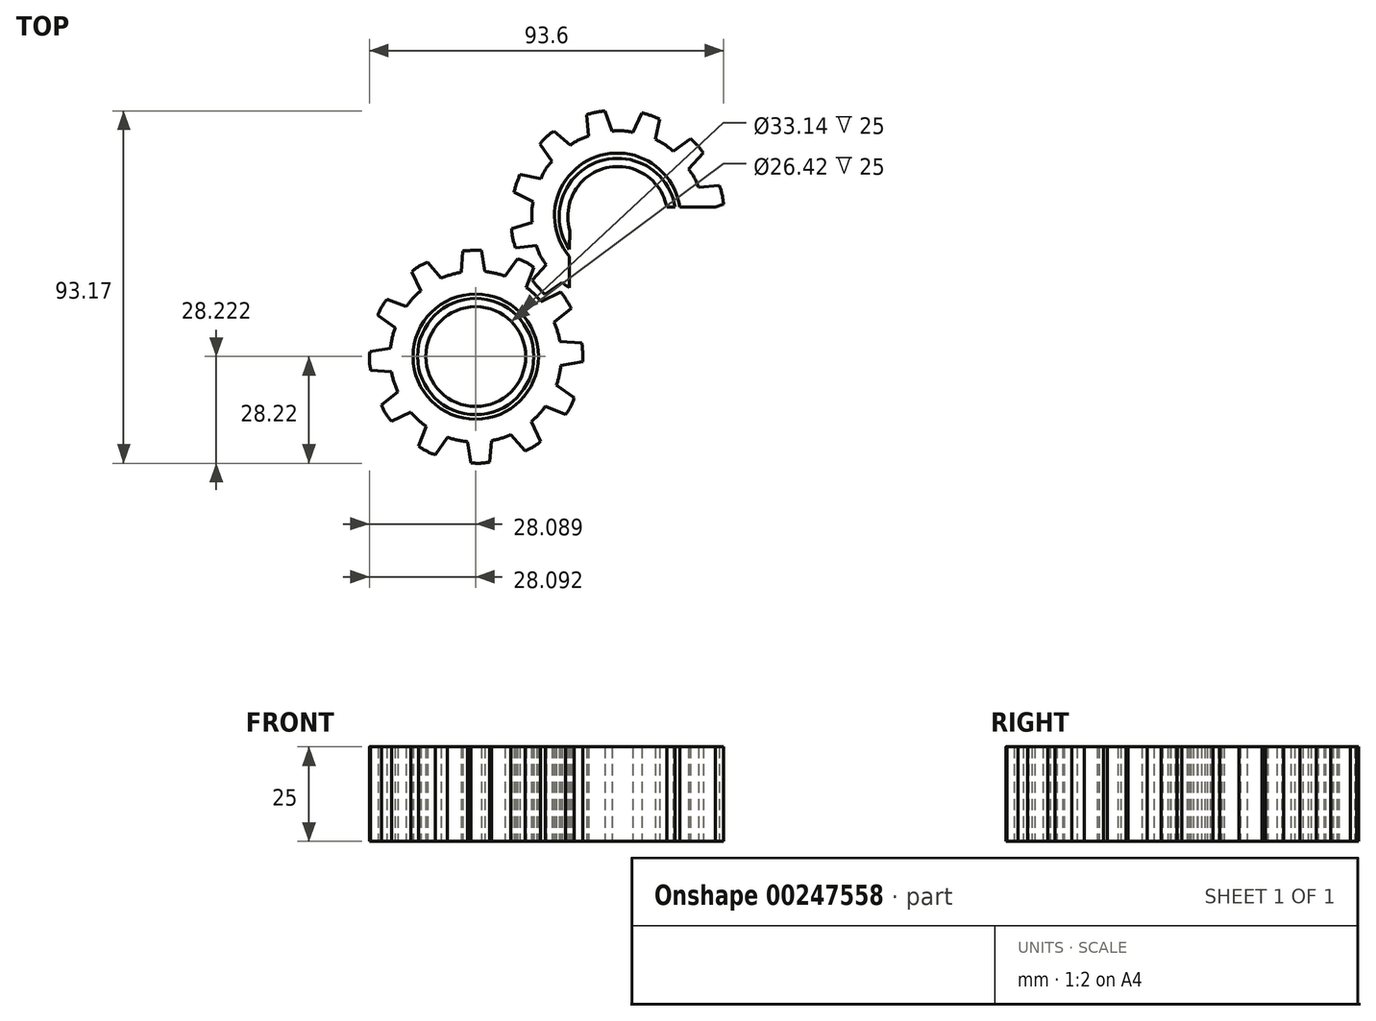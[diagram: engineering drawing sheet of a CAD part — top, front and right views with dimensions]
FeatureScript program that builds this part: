
annotation { "Feature Type Name" : "Feature", "Feature Type Description" : "" }
export const myFeature = defineFeature(function(context is Context, id is Id, definition is map)
    precondition{}
    {
        {
            var Q0;
            Q0=qCreatedBy(makeId("Top.planeOp"),FACE);
            var sketch = newSketch(context, id + "F0", { "sketchPlane" : qUnion([Q0])});
            skPoint(sketch, "E0", {"position": v(-30.45, 10.62) * mm});
            skPoint(sketch, "E1", {"position": v(-30.54, 5.58) * mm});
            skPoint(sketch, "E2", {"position": v(-30.54, 3.71) * mm});
            skPoint(sketch, "E3", {"position": v(-30.54, -4.5) * mm});
            skPoint(sketch, "E4", {"position": v(-4.8, 16.75) * mm});
            skPoint(sketch, "E5", {"position": v(-2.6, 16.75) * mm});
            skPoint(sketch, "E6", {"position": v(-1.42, 16.75) * mm});
            skPoint(sketch, "E7", {"position": v(8.01, 16.75) * mm});
            skPoint(sketch, "E8", {"position": v(10.19, 17.58) * mm});
            skPoint(sketch, "E9", {"position": v(9.1, 22.45) * mm});
            skPoint(sketch, "E10", {"position": v(3.62, 21.97) * mm});
            skPoint(sketch, "E11", {"position": v(0.93, 26.8) * mm});
            skPoint(sketch, "E12", {"position": v(4.81, 31.12) * mm});
            skPoint(sketch, "E13", {"position": v(1.46, 34.84) * mm});
            skPoint(sketch, "E14", {"position": v(-3.18, 31.55) * mm});
            skPoint(sketch, "E15", {"position": v(-7.79, 34.66) * mm});
            skPoint(sketch, "E16", {"position": v(-6.65, 40.1) * mm});
            skPoint(sketch, "E17", {"position": v(-11.41, 41.7) * mm});
            skPoint(sketch, "E18", {"position": v(-13.75, 36.5) * mm});
            skPoint(sketch, "E19", {"position": v(-19.29, 36.84) * mm});
            skPoint(sketch, "E20", {"position": v(-21.12, 42.19) * mm});
            skPoint(sketch, "E21", {"position": v(-26.03, 41.2) * mm});
            skPoint(sketch, "E22", {"position": v(-25.51, 35.54) * mm});
            skPoint(sketch, "E23", {"position": v(-30.37, 33.11) * mm});
            skPoint(sketch, "E24", {"position": v(-34.69, 36.84) * mm});
            skPoint(sketch, "E25", {"position": v(-38.36, 33.48) * mm});
            skPoint(sketch, "E26", {"position": v(-35.15, 28.85) * mm});
            skPoint(sketch, "E27", {"position": v(-38.07, 24.3) * mm});
            skPoint(sketch, "E28", {"position": v(-43.6, 25.41) * mm});
            skPoint(sketch, "E29", {"position": v(-45.2, 20.68) * mm});
            skPoint(sketch, "E30", {"position": v(-40.11, 18.23) * mm});
            skPoint(sketch, "E31", {"position": v(-40.4, 12.78) * mm});
            skPoint(sketch, "E32", {"position": v(-45.77, 11.02) * mm});
            skPoint(sketch, "E33", {"position": v(-44.74, 6.06) * mm});
            skPoint(sketch, "E34", {"position": v(-39.26, 6.63) * mm});
            skPoint(sketch, "E35", {"position": v(-36.68, 1.59) * mm});
            skPoint(sketch, "E36", {"position": v(-40.4, -2.55) * mm});
            skPoint(sketch, "E37", {"position": v(-37.07, -6.32) * mm});
            skPoint(sketch, "E38", {"position": v(-32.47, -3.12) * mm});
            skLineSegment(sketch, "E39", {"start": v(-30.45, 10.62) * mm, "end": v(-30.54, 5.58) * mm});
            skLineSegment(sketch, "E40", {"start": v(-30.54, 3.71) * mm, "end": v(-30.54, -4.5) * mm});
            skLineSegment(sketch, "E41", {"start": v(-4.8, 16.75) * mm, "end": v(-2.6, 16.75) * mm});
            skLineSegment(sketch, "E42", {"start": v(-1.42, 16.75) * mm, "end": v(8.01, 16.75) * mm});
            skLineSegment(sketch, "E43", {"start": v(8.01, 16.75) * mm, "end": v(10.19, 17.58) * mm});
            skLineSegment(sketch, "E44", {"start": v(3.62, 21.97) * mm, "end": v(9.1, 22.45) * mm});
            skLineSegment(sketch, "E45", {"start": v(0.93, 26.8) * mm, "end": v(4.81, 31.12) * mm});
            skLineSegment(sketch, "E46", {"start": v(1.46, 34.84) * mm, "end": v(-3.18, 31.55) * mm});
            skLineSegment(sketch, "E47", {"start": v(-6.65, 40.1) * mm, "end": v(-7.79, 34.66) * mm});
            skLineSegment(sketch, "E48", {"start": v(-11.41, 41.7) * mm, "end": v(-13.75, 36.5) * mm});
            skLineSegment(sketch, "E49", {"start": v(-21.12, 42.19) * mm, "end": v(-19.29, 36.84) * mm});
            skLineSegment(sketch, "E50", {"start": v(-26.03, 41.2) * mm, "end": v(-25.51, 35.54) * mm});
            skLineSegment(sketch, "E51", {"start": v(-34.69, 36.84) * mm, "end": v(-30.37, 33.11) * mm});
            skLineSegment(sketch, "E52", {"start": v(-38.36, 33.48) * mm, "end": v(-35.15, 28.85) * mm});
            skLineSegment(sketch, "E53", {"start": v(-43.6, 25.41) * mm, "end": v(-38.07, 24.3) * mm});
            skLineSegment(sketch, "E54", {"start": v(-45.2, 20.68) * mm, "end": v(-40.11, 18.23) * mm});
            skLineSegment(sketch, "E55", {"start": v(-45.77, 11.02) * mm, "end": v(-40.4, 12.78) * mm});
            skLineSegment(sketch, "E56", {"start": v(-39.26, 6.63) * mm, "end": v(-44.74, 6.06) * mm});
            skLineSegment(sketch, "E57", {"start": v(-36.68, 1.59) * mm, "end": v(-40.4, -2.55) * mm});
            skLineSegment(sketch, "E58", {"start": v(-32.47, -3.12) * mm, "end": v(-37.07, -6.32) * mm});
            skArc(sketch, "E59", {"start": v(-32.47, -3.12) * mm, "mid": v(-31.54, -3.87) * mm, "end": v(-30.54, -4.5) * mm});
            skArc(sketch, "E60", {"start": v(-40.4, -2.55) * mm, "mid": v(-38.8, -4.49) * mm, "end": v(-37.07, -6.32) * mm});
            skArc(sketch, "E61", {"start": v(-39.26, 6.63) * mm, "mid": v(-38.26, 3.96) * mm, "end": v(-36.68, 1.59) * mm});
            skArc(sketch, "E62", {"start": v(-45.77, 11.02) * mm, "mid": v(-45.52, 8.48) * mm, "end": v(-44.74, 6.06) * mm});
            skArc(sketch, "E63", {"start": v(-40.11, 18.23) * mm, "mid": v(-40.5, 15.52) * mm, "end": v(-40.4, 12.78) * mm});
            skArc(sketch, "E64", {"start": v(-43.6, 25.41) * mm, "mid": v(-44.5, 23.08) * mm, "end": v(-45.2, 20.68) * mm});
            skArc(sketch, "E65", {"start": v(-35.15, 28.85) * mm, "mid": v(-36.86, 26.74) * mm, "end": v(-38.07, 24.3) * mm});
            skArc(sketch, "E66", {"start": v(-34.69, 36.84) * mm, "mid": v(-36.67, 35.31) * mm, "end": v(-38.36, 33.48) * mm});
            skArc(sketch, "E67", {"start": v(-25.51, 35.54) * mm, "mid": v(-28.05, 34.55) * mm, "end": v(-30.37, 33.11) * mm});
            skArc(sketch, "E68", {"start": v(-21.12, 42.19) * mm, "mid": v(-23.6, 41.85) * mm, "end": v(-26.03, 41.2) * mm});
            skArc(sketch, "E69", {"start": v(-13.75, 36.5) * mm, "mid": v(-16.5, 36.97) * mm, "end": v(-19.29, 36.84) * mm});
            skArc(sketch, "E70", {"start": v(-6.65, 40.1) * mm, "mid": v(-9, 41) * mm, "end": v(-11.41, 41.7) * mm});
            skArc(sketch, "E71", {"start": v(3.62, 21.97) * mm, "mid": v(2.52, 24.51) * mm, "end": v(0.93, 26.8) * mm});
            skArc(sketch, "E72", {"start": v(-3.18, 31.55) * mm, "mid": v(-5.34, 33.31) * mm, "end": v(-7.79, 34.66) * mm});
            skArc(sketch, "E73", {"start": v(-1.42, 16.75) * mm, "mid": v(-24.66, 29.62) * mm, "end": v(-30.54, 3.71) * mm});
            skArc(sketch, "E74", {"start": v(-2.6, 16.75) * mm, "mid": v(-23.52, 28.57) * mm, "end": v(-30.54, 5.58) * mm});
            skArc(sketch, "E75", {"start": v(-4.8, 16.75) * mm, "mid": v(-20.85, 27.15) * mm, "end": v(-30.45, 10.62) * mm});
            skArc(sketch, "E76", {"start": v(4.81, 31.12) * mm, "mid": v(3.27, 33.1) * mm, "end": v(1.46, 34.84) * mm});
            skArc(sketch, "E77", {"start": v(10.19, 17.58) * mm, "mid": v(9.82, 20.05) * mm, "end": v(9.1, 22.45) * mm});
            skSolve(sketch);
        }
        {
            var Q0;
            Q0=qCreatedBy(makeId("Top.planeOp"),FACE);
            var sketch = newSketch(context, id + "F1", { "sketchPlane" : qUnion([Q0])});
            skPoint(sketch, "E78", {"position": v(-55.32, -22.76) * mm});
            skPoint(sketch, "E79", {"position": v(-55.32, -9.56) * mm});
            skPoint(sketch, "E80", {"position": v(-55.32, -7.4) * mm});
            skPoint(sketch, "E81", {"position": v(-55.32, -6.19) * mm});
            skPoint(sketch, "E82", {"position": v(-53.8, 5.36) * mm});
            skPoint(sketch, "E83", {"position": v(-58.8, 5.17) * mm});
            skPoint(sketch, "E84", {"position": v(-68.06, 2.19) * mm});
            skPoint(sketch, "E85", {"position": v(-72.25, -0.4) * mm});
            skPoint(sketch, "E86", {"position": v(-78.82, -7.58) * mm});
            skPoint(sketch, "E87", {"position": v(-81.16, -11.85) * mm});
            skPoint(sketch, "E88", {"position": v(-83.27, -21.4) * mm});
            skPoint(sketch, "E89", {"position": v(-83.08, -26.38) * mm});
            skPoint(sketch, "E90", {"position": v(-80.2, -35.59) * mm});
            skPoint(sketch, "E91", {"position": v(-77.58, -39.8) * mm});
            skPoint(sketch, "E92", {"position": v(-70.45, -46.42) * mm});
            skPoint(sketch, "E93", {"position": v(-66, -48.76) * mm});
            skPoint(sketch, "E94", {"position": v(-62.84, -44.1) * mm});
            skPoint(sketch, "E95", {"position": v(-56.55, -50.87) * mm});
            skPoint(sketch, "E96", {"position": v(-51.66, -50.66) * mm});
            skPoint(sketch, "E97", {"position": v(-42.3, -47.78) * mm});
            skPoint(sketch, "E98", {"position": v(-38.14, -45.2) * mm});
            skPoint(sketch, "E99", {"position": v(-31.55, -38.03) * mm});
            skPoint(sketch, "E100", {"position": v(-29.28, -33.58) * mm});
            skPoint(sketch, "E101", {"position": v(-27.06, -24.12) * mm});
            skPoint(sketch, "E102", {"position": v(-27.24, -19.21) * mm});
            skPoint(sketch, "E103", {"position": v(-30.08, -10) * mm});
            skPoint(sketch, "E104", {"position": v(-32.82, -5.71) * mm});
            skPoint(sketch, "E105", {"position": v(-40.02, 0.77) * mm});
            skPoint(sketch, "E106", {"position": v(-44.34, 3.06) * mm});
            skCircle(sketch, "E107", {"center": v(-55.32, -22.76) * mm, "radius": 16.57 * mm});
            skArc(sketch, "E108", {"start": v(-69.87, -5.42) * mm, "mid": v(-71.92, -7.37) * mm, "end": v(-73.7, -9.56) * mm});
            skPoint(sketch, "E109", {"position": v(-59.08, -0.44) * mm});
            skPoint(sketch, "E110", {"position": v(-52.95, -0.25) * mm});
            skPoint(sketch, "E111", {"position": v(-64.49, -2.06) * mm});
            skPoint(sketch, "E112", {"position": v(-69.87, -5.42) * mm});
            skPoint(sketch, "E113", {"position": v(-73.7, -9.56) * mm});
            skPoint(sketch, "E114", {"position": v(-76.6, -15.05) * mm});
            skPoint(sketch, "E115", {"position": v(-77.85, -20.56) * mm});
            skPoint(sketch, "E116", {"position": v(-77.58, -26.82) * mm});
            skPoint(sketch, "E117", {"position": v(-75.92, -32.12) * mm});
            skPoint(sketch, "E118", {"position": v(-72.51, -37.48) * mm});
            skPoint(sketch, "E119", {"position": v(-68.45, -41.2) * mm});
            skPoint(sketch, "E120", {"position": v(-57.54, -45.28) * mm});
            skPoint(sketch, "E121", {"position": v(-51.1, -45) * mm});
            skPoint(sketch, "E122", {"position": v(-46, -43.4) * mm});
            skPoint(sketch, "E123", {"position": v(-40.57, -39.93) * mm});
            skPoint(sketch, "E124", {"position": v(-36.92, -35.95) * mm});
            skPoint(sketch, "E125", {"position": v(-33.98, -30.3) * mm});
            skPoint(sketch, "E126", {"position": v(-32.8, -25.15) * mm});
            skPoint(sketch, "E127", {"position": v(-33.05, -18.72) * mm});
            skPoint(sketch, "E128", {"position": v(-34.6, -13.63) * mm});
            skPoint(sketch, "E129", {"position": v(-38, -8.17) * mm});
            skPoint(sketch, "E130", {"position": v(-41.94, -4.5) * mm});
            skPoint(sketch, "E131", {"position": v(-47.6, -1.48) * mm});
            skLineSegment(sketch, "E132", {"start": v(-53.8, 5.36) * mm, "end": v(-52.95, -0.25) * mm});
            skLineSegment(sketch, "E133", {"start": v(-58.8, 5.17) * mm, "end": v(-59.08, -0.44) * mm});
            skLineSegment(sketch, "E134", {"start": v(-68.06, 2.19) * mm, "end": v(-64.49, -2.06) * mm});
            skLineSegment(sketch, "E135", {"start": v(-72.25, -0.4) * mm, "end": v(-69.87, -5.42) * mm});
            skLineSegment(sketch, "E136", {"start": v(-78.82, -7.58) * mm, "end": v(-73.7, -9.56) * mm});
            skLineSegment(sketch, "E137", {"start": v(-81.16, -11.85) * mm, "end": v(-76.6, -15.05) * mm});
            skLineSegment(sketch, "E138", {"start": v(-83.27, -21.4) * mm, "end": v(-77.85, -20.56) * mm});
            skLineSegment(sketch, "E139", {"start": v(-83.08, -26.38) * mm, "end": v(-77.58, -26.82) * mm});
            skLineSegment(sketch, "E140", {"start": v(-80.2, -35.59) * mm, "end": v(-75.92, -32.12) * mm});
            skLineSegment(sketch, "E141", {"start": v(-77.58, -39.8) * mm, "end": v(-72.51, -37.48) * mm});
            skLineSegment(sketch, "E142", {"start": v(-68.45, -41.2) * mm, "end": v(-70.45, -46.42) * mm});
            skLineSegment(sketch, "E143", {"start": v(-62.84, -44.1) * mm, "end": v(-66, -48.76) * mm});
            skLineSegment(sketch, "E144", {"start": v(-57.54, -45.28) * mm, "end": v(-56.55, -50.87) * mm});
            skLineSegment(sketch, "E145", {"start": v(-51.1, -45) * mm, "end": v(-51.66, -50.66) * mm});
            skLineSegment(sketch, "E146", {"start": v(-46, -43.4) * mm, "end": v(-42.3, -47.78) * mm});
            skLineSegment(sketch, "E147", {"start": v(-40.57, -39.93) * mm, "end": v(-38.14, -45.2) * mm});
            skLineSegment(sketch, "E148", {"start": v(-36.92, -35.95) * mm, "end": v(-31.55, -38.03) * mm});
            skLineSegment(sketch, "E149", {"start": v(-33.98, -30.3) * mm, "end": v(-29.28, -33.58) * mm});
            skLineSegment(sketch, "E150", {"start": v(-32.8, -25.15) * mm, "end": v(-27.06, -24.12) * mm});
            skLineSegment(sketch, "E151", {"start": v(-33.05, -18.72) * mm, "end": v(-27.24, -19.21) * mm});
            skLineSegment(sketch, "E152", {"start": v(-34.6, -13.63) * mm, "end": v(-30.08, -10) * mm});
            skLineSegment(sketch, "E153", {"start": v(-38, -8.17) * mm, "end": v(-32.82, -5.71) * mm});
            skLineSegment(sketch, "E154", {"start": v(-41.94, -4.5) * mm, "end": v(-40.02, 0.77) * mm});
            skLineSegment(sketch, "E155", {"start": v(-44.34, 3.06) * mm, "end": v(-47.6, -1.48) * mm});
            skArc(sketch, "E156.trimOffspring", {"start": v(-76.6, -15.05) * mm, "mid": v(-77.4, -17.77) * mm, "end": v(-77.85, -20.56) * mm});
            skArc(sketch, "E157.trimOffspring", {"start": v(-77.58, -26.82) * mm, "mid": v(-76.92, -29.52) * mm, "end": v(-75.92, -32.12) * mm});
            skArc(sketch, "E158.trimOffspring", {"start": v(-72.51, -37.48) * mm, "mid": v(-70.6, -39.46) * mm, "end": v(-68.45, -41.2) * mm});
            skArc(sketch, "E159.trimOffspring", {"start": v(-62.84, -44.1) * mm, "mid": v(-60.23, -44.86) * mm, "end": v(-57.54, -45.28) * mm});
            skArc(sketch, "E160.trimOffspring", {"start": v(-51.1, -45) * mm, "mid": v(-48.5, -44.34) * mm, "end": v(-46, -43.4) * mm});
            skArc(sketch, "E161.trimOffspring", {"start": v(-40.57, -39.93) * mm, "mid": v(-38.63, -38.05) * mm, "end": v(-36.92, -35.95) * mm});
            skArc(sketch, "E162.trimOffspring", {"start": v(-33.98, -30.3) * mm, "mid": v(-33.24, -27.76) * mm, "end": v(-32.8, -25.15) * mm});
            skArc(sketch, "E163.trimOffspring", {"start": v(-33.05, -18.72) * mm, "mid": v(-33.68, -16.12) * mm, "end": v(-34.6, -13.63) * mm});
            skArc(sketch, "E164.trimOffspring", {"start": v(-38, -8.17) * mm, "mid": v(-39.86, -6.22) * mm, "end": v(-41.94, -4.5) * mm});
            skArc(sketch, "E165.trimOffspring", {"start": v(-47.6, -1.48) * mm, "mid": v(-50.24, -0.7) * mm, "end": v(-52.95, -0.25) * mm});
            skArc(sketch, "E166.trimOffspring", {"start": v(-59.08, -0.44) * mm, "mid": v(-61.84, -1.08) * mm, "end": v(-64.49, -2.06) * mm});
            skArc(sketch, "E167", {"start": v(-53.8, 5.36) * mm, "mid": v(-56.3, 5.31) * mm, "end": v(-58.8, 5.17) * mm});
            skArc(sketch, "E168", {"start": v(-68.06, 2.19) * mm, "mid": v(-70.3, 1.13) * mm, "end": v(-72.25, -0.4) * mm});
            skArc(sketch, "E169", {"start": v(-78.82, -7.58) * mm, "mid": v(-80.17, -9.61) * mm, "end": v(-81.16, -11.85) * mm});
            skArc(sketch, "E170", {"start": v(-83.27, -21.4) * mm, "mid": v(-83.4, -23.9) * mm, "end": v(-83.08, -26.38) * mm});
            skArc(sketch, "E171", {"start": v(-80.2, -35.59) * mm, "mid": v(-79.13, -37.84) * mm, "end": v(-77.58, -39.8) * mm});
            skArc(sketch, "E172", {"start": v(-70.45, -46.42) * mm, "mid": v(-68.31, -47.77) * mm, "end": v(-66, -48.76) * mm});
            skArc(sketch, "E173", {"start": v(-56.55, -50.87) * mm, "mid": v(-54.1, -50.97) * mm, "end": v(-51.66, -50.66) * mm});
            skArc(sketch, "E174", {"start": v(-42.3, -47.78) * mm, "mid": v(-40.13, -46.64) * mm, "end": v(-38.14, -45.2) * mm});
            skArc(sketch, "E175", {"start": v(-31.55, -38.03) * mm, "mid": v(-30.18, -35.92) * mm, "end": v(-29.28, -33.58) * mm});
            skArc(sketch, "E176", {"start": v(-27.06, -24.12) * mm, "mid": v(-27.04, -21.66) * mm, "end": v(-27.24, -19.21) * mm});
            skArc(sketch, "E177", {"start": v(-30.08, -10) * mm, "mid": v(-31.35, -7.79) * mm, "end": v(-32.82, -5.71) * mm});
            skArc(sketch, "E178", {"start": v(-40.02, 0.77) * mm, "mid": v(-42.04, 2.19) * mm, "end": v(-44.34, 3.06) * mm});
            skSolve(sketch);
        }
        {
            var Q0;
            Q0=qCreatedBy(makeId("Top.planeOp"),FACE);
            var sketch = newSketch(context, id + "F2", { "sketchPlane" : qUnion([Q0])});
            skPoint(sketch, "E179", {"position": v(-55.32, -22.76) * mm});
            skPoint(sketch, "E180", {"position": v(-55.31, -9.55) * mm});
            skPoint(sketch, "E181", {"position": v(-55.31, -7.39) * mm});
            skCircle(sketch, "E182", {"center": v(-55.32, -22.76) * mm, "radius": 15.37 * mm});
            skCircle(sketch, "E183", {"center": v(-55.32, -22.76) * mm, "radius": 13.2 * mm});
            skSolve(sketch);
        }
        {
            var Q0;
            Q0 = qSketchRegion(id + "F0", true);
            var Q1;
            Q1=makeQuery(id+"F1.imprint","IMPRINT",FACE,{"disambiguationData":[TD([[makeQuery(id+"F1.imprint","IMPRINT",EDGE,{"derivedFrom":sQuery(id+"F1.wireOp",EDGE,"E107")}),-1.0]])]});
            var Q2;
            Q2 = qSketchRegion(id + "F2", true);
            extrude(context, id + "F3", {"entities" : qUnion([Q0, Q1, Q2]), "depth" : 25 * mm});
        }
    });
